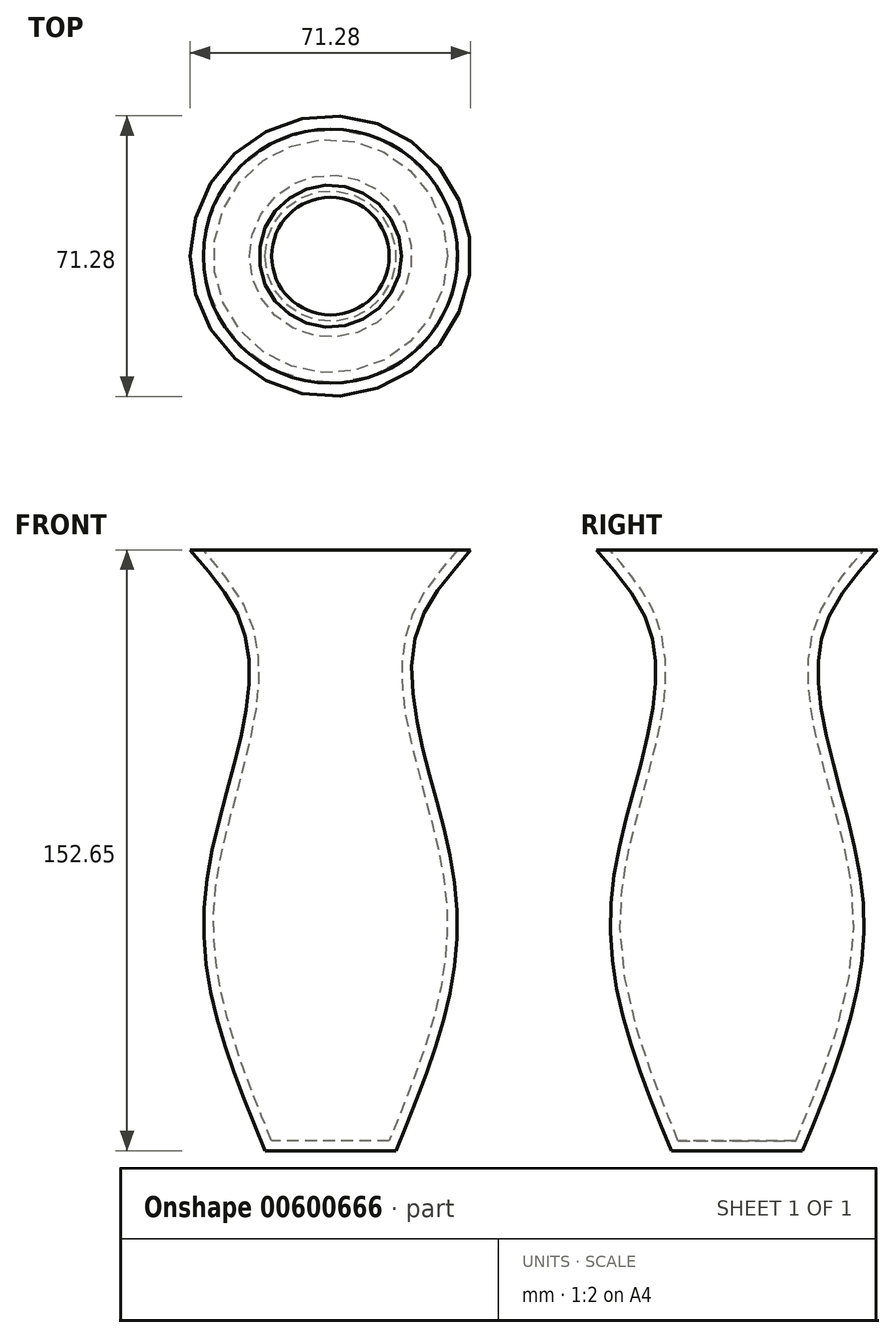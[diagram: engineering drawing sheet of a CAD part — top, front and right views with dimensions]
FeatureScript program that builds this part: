
annotation { "Feature Type Name" : "Feature", "Feature Type Description" : "" }
export const myFeature = defineFeature(function(context is Context, id is Id, definition is map)
    precondition{}
    {
        {
            var Q0;
            Q0=qCreatedBy(makeId("Top.planeOp"),FACE);
            var sketch = newSketch(context, id + "F0", { "sketchPlane" : qUnion([Q0])});
            skCircle(sketch, "E0", {"center": v(0, 0) * mm, "radius": 14.94 * mm});
            skSolve(sketch);
        }
        {
            var Q0;
            Q0=qCreatedBy(makeId("Top.planeOp"),FACE);
            cPlane(context, id + "F1", {"entities" : qUnion([Q0]), "cplaneType" : CPlaneType.OFFSET, "offset" : 61.47 * mm, "width" : 152.4 * mm, "height" : 152.4 * mm});
        }
        {
            var Q0;
            Q0=qCreatedBy(id+"F1.planeOp",FACE);
            var sketch = newSketch(context, id + "F2", { "sketchPlane" : qUnion([Q0])});
            skCircle(sketch, "E1", {"center": v(0, 0) * mm, "radius": 29.43 * mm});
            skSolve(sketch);
        }
        {
            var Q0;
            Q0=qCreatedBy(id+"F1.planeOp",FACE);
            cPlane(context, id + "F3", {"entities" : qUnion([Q0]), "cplaneType" : CPlaneType.OFFSET, "offset" : 73.4 * mm, "width" : 152.4 * mm, "height" : 152.4 * mm});
        }
        {
            var Q0;
            Q0=qCreatedBy(id+"F3.planeOp",FACE);
            var sketch = newSketch(context, id + "F4", { "sketchPlane" : qUnion([Q0])});
            skCircle(sketch, "E2", {"center": v(0, 0) * mm, "radius": 21.34 * mm});
            skSolve(sketch);
        }
        {
            var Q0;
            Q0=qCreatedBy(id+"F3.planeOp",FACE);
            cPlane(context, id + "F5", {"entities" : qUnion([Q0]), "cplaneType" : CPlaneType.OFFSET, "offset" : 15.24 * mm, "width" : 152.4 * mm, "height" : 152.4 * mm});
        }
        {
            var Q0;
            Q0=qCreatedBy(id+"F5.planeOp",FACE);
            var sketch = newSketch(context, id + "F6", { "sketchPlane" : qUnion([Q0])});
            skCircle(sketch, "E3", {"center": v(0, 0) * mm, "radius": 32.3 * mm});
            skSolve(sketch);
        }
        {
            var Q0;
            Q0=makeQuery(id+"F6.imprint","IMPRINT",FACE,{"disambiguationData":[TD([[makeQuery(id+"F6.imprint","IMPRINT",EDGE,{"derivedFrom":sQuery(id+"F6.wireOp",EDGE,"E3")}),1.0]])]});
            var Q1;
            Q1=makeQuery(id+"F4.imprint","IMPRINT",FACE,{"disambiguationData":[TD([[makeQuery(id+"F4.imprint","IMPRINT",EDGE,{"derivedFrom":sQuery(id+"F4.wireOp",EDGE,"E2")}),1.0]])]});
            var Q2;
            Q2=makeQuery(id+"F2.imprint","IMPRINT",FACE,{"disambiguationData":[TD([[makeQuery(id+"F2.imprint","IMPRINT",EDGE,{"derivedFrom":sQuery(id+"F2.wireOp",EDGE,"E1")}),1.0]])]});
            var Q3;
            Q3=makeQuery(id+"F0.imprint","IMPRINT",FACE,{"disambiguationData":[TD([[makeQuery(id+"F0.imprint","IMPRINT",EDGE,{"derivedFrom":sQuery(id+"F0.wireOp",EDGE,"E0")}),1.0]])]});
            loft(context, id + "F7", {"sheetProfilesArray" : [{ "sheetProfileEntities" : qUnion([Q0]) }, { "sheetProfileEntities" : qUnion([Q1]) }, { "sheetProfileEntities" : qUnion([Q2]) }, { "sheetProfileEntities" : qUnion([Q3]) }]});
        }
        {
            var Q0;
            Q0=makeQuery(id+"F7.opLoft","CAP_FACE",FACE,{"disambiguationData":[OSD([makeQuery(id+"F6.imprint","IMPRINT",FACE,{"disambiguationData":[TD([[makeQuery(id+"F6.imprint","IMPRINT",EDGE,{"derivedFrom":sQuery(id+"F6.wireOp",EDGE,"E3")}),1.0]])]})])],"isStart":true});
            shell(context, id + "F8", {"entities" : qUnion([Q0]), "thickness" : 2.54 * mm, "oppositeDirection" : true});
        }
    });
